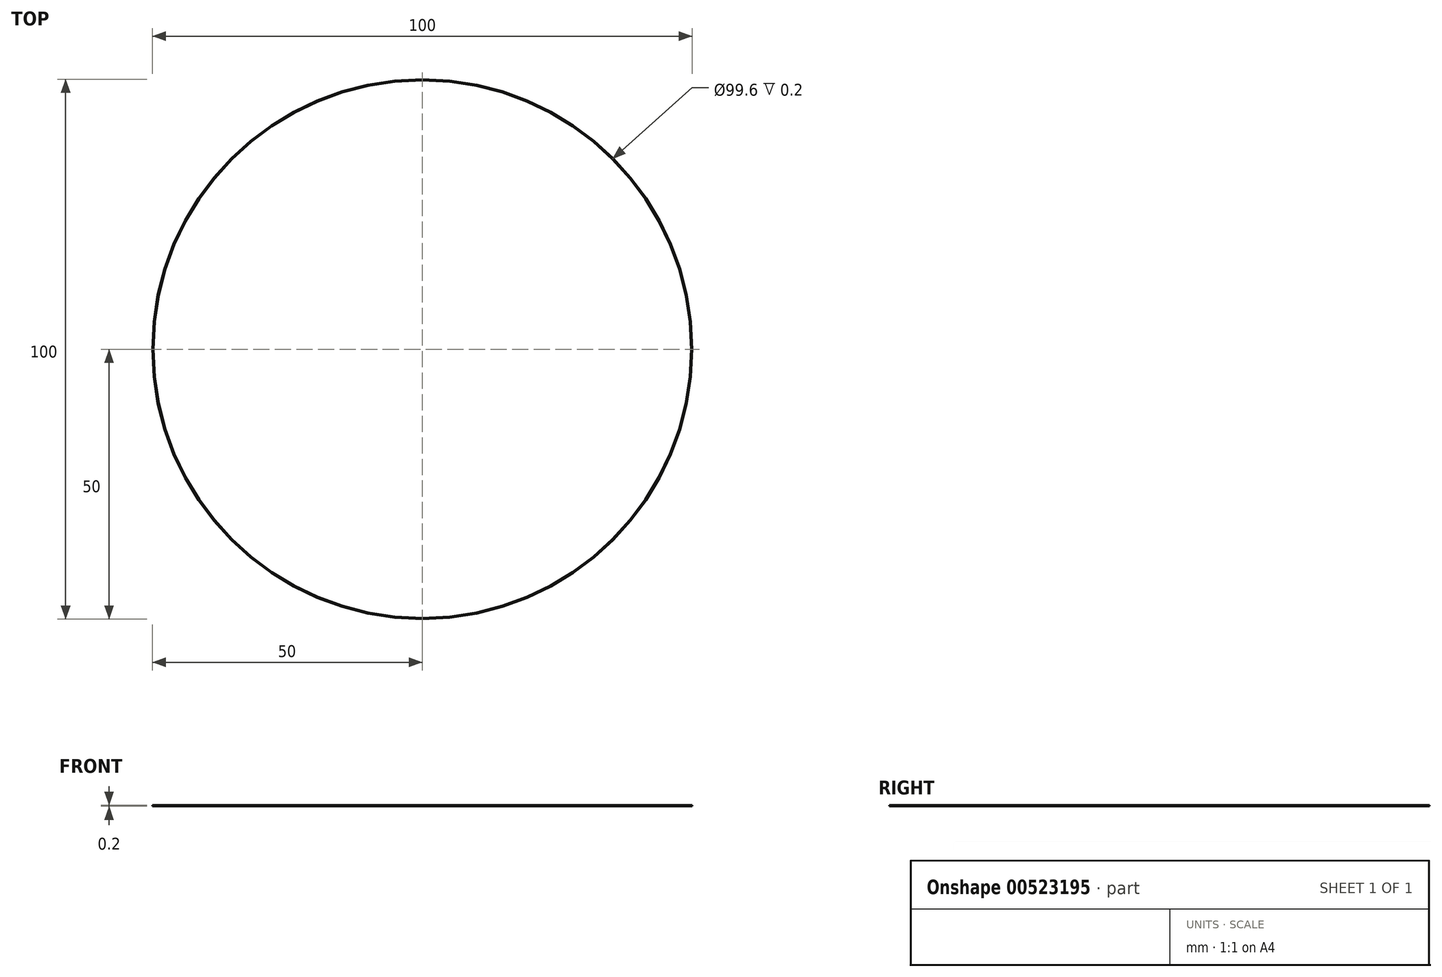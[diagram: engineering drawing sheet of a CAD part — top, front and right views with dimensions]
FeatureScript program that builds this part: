
annotation { "Feature Type Name" : "Feature", "Feature Type Description" : "" }
export const myFeature = defineFeature(function(context is Context, id is Id, definition is map)
    precondition{}
    {
        {
            var Q0;
            Q0=qCreatedBy(makeId("Top.planeOp"),FACE);
            var sketch = newSketch(context, id + "F0", { "sketchPlane" : qUnion([Q0])});
            skCircle(sketch, "E0", {"center": v(0, 0) * mm, "radius": 50 * mm});
            skCircle(sketch, "E1.0", {"center": v(0, 0) * mm, "radius": 49.8 * mm});
            skSolve(sketch);
        }
        {
            var Q0;
            Q0=makeQuery(id+"F0.imprint","IMPRINT",FACE,{"disambiguationData":[TD([[makeQuery(id+"F0.imprint","IMPRINT",EDGE,{"derivedFrom":sQuery(id+"F0.wireOp",EDGE,"E0")}),1.0]])]});
            extrude(context, id + "F1", {"entities" : qUnion([Q0]), "depth" : .2 * mm, "offsetDistance" : 25 * mm});
        }
    });
